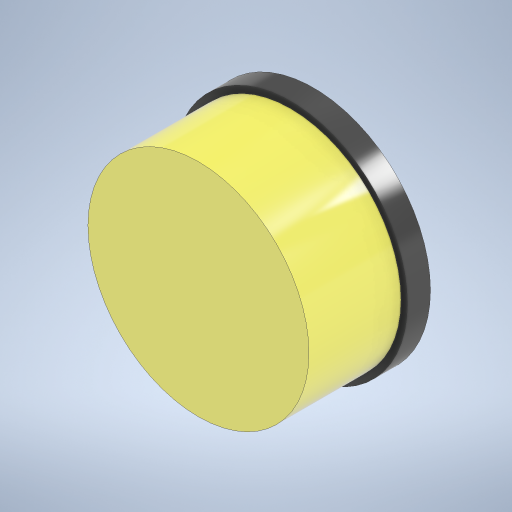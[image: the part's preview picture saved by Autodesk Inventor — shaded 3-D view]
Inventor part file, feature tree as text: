
AUTODESK INVENTOR PART (.ipt)
format: ipt  version: 2023 (Build 270158000, 158)  size: 253,952 bytes
history: native  units: in
note: dims shown in document units (in); Inventor stores cm internally (conversion verified against a paired STEP export)
features: extrude x2, sketch x2
ambient origin geometry x8: Origin, YZ Plane, XZ Plane, XY Plane, X Axis, Y Axis, Z Axis, Center Point
bodies: Solid1 (feature_tree)
feature tree (4):
  extrude  "Extrusion1"  Depth=0.1969in TaperAngle=0.0deg
  extrude  "Extrusion2"  [1 undecoded]
  sketch  "Sketch1"  dims[d0=2.0in d1=0.1969in d2=0.0in]
  sketch  "Sketch2"  dims[d3=0.7874in d4=0.0in]
note: 1 required parameter value undecoded (feature->parameter linkage not recoverable at this tier; creation-order binding heuristic only, values carry confidence <= 0.55)
